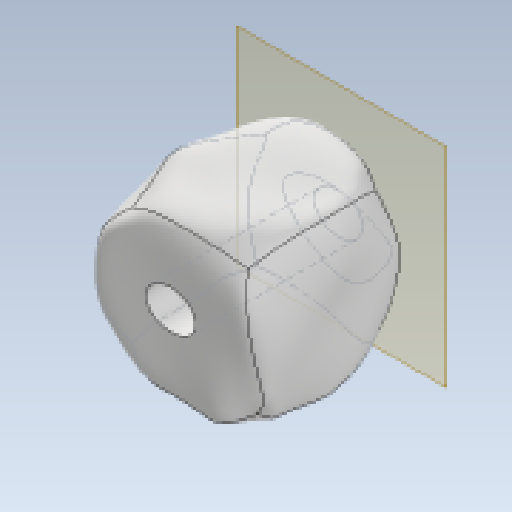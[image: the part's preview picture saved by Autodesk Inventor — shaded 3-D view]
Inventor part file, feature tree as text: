
AUTODESK INVENTOR PART (.ipt)
format: ipt  version: 2023 (Build 270158030, 158C)  size: 741,888 bytes
history: native  units: mm
features: other x7, plane x4, extrude x2, sketch x2, revolve x1, surface_op x1, reference x1
ambient origin geometry x8: Origin, YZ Plane, XZ Plane, XY Plane, X Axis, Y Axis, Z Axis, Center Point
bodies: Solid1 (feature_tree), Solid4 (feature_tree)
feature tree (18):
  revolve  "Revolution1"  [1 undecoded]
  plane  "Work Plane1"
  plane  "Work Plane2"
  other  "Form7"
  surface_op  "Replace Face4"
  extrude  "Extrusion1"  Depth=30.0mm TaperAngle=0.0deg
  plane  "Work Plane6"
  extrude  "Extrusion3"  Depth=2.5mm
  sketch  "Sketch1"  dims[d0=25.0mm d1=12.0mm]
  reference  "Reference1"
  plane  "Work Plane5"
  sketch  "Sketch5"  dims[d2=90.0deg d4=30.0mm d5=0.0mm d6=2.5mm d7=3.0mm d20=1.0mm d21=0.0mm]
  other  "<userpath>\Documents\0004-inventor\3D-CAD-main\trebuchet\trebuchet-assembly.iam"
  other  "trebuchet-assembly.iam"
  other  "V1_baseplate:1"
  other  "<userpath>\Documents\0004-inventor\3D-CAD-main\trebuchet\V4.0-trebuchet-printable.iam"
  other  "V4.0-trebuchet-printable.iam"
  other  "border:1"
note: 1 required parameter value undecoded (feature->parameter linkage not recoverable at this tier; creation-order binding heuristic only, values carry confidence <= 0.55)
